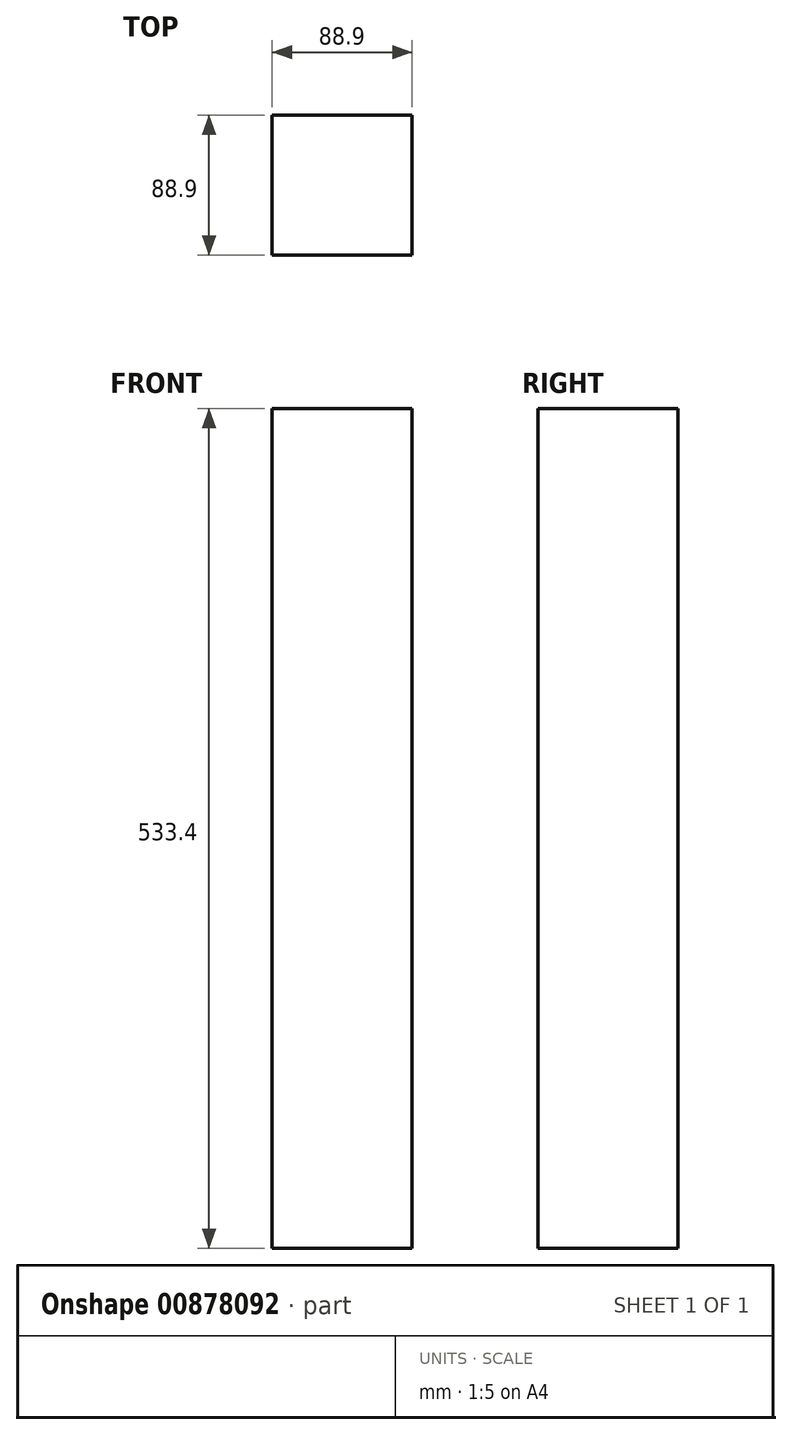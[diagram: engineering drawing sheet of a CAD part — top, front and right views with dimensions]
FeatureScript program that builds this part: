
annotation { "Feature Type Name" : "Feature", "Feature Type Description" : "" }
export const myFeature = defineFeature(function(context is Context, id is Id, definition is map)
    precondition{}
    {
        {
            var Q0;
            Q0=qCreatedBy(makeId("Top.planeOp"),FACE);
            var sketch = newSketch(context, id + "F0", { "sketchPlane" : qUnion([Q0])});
            skLineSegment(sketch, "E0.bottom", {"start": v(44.45, 44.45) * mm, "end": v(-44.45, 44.45) * mm});
            skLineSegment(sketch, "E0.top", {"start": v(44.45, -44.45) * mm, "end": v(-44.45, -44.45) * mm});
            skLineSegment(sketch, "E0.left", {"start": v(44.45, 44.45) * mm, "end": v(44.45, -44.45) * mm});
            skLineSegment(sketch, "E0.right", {"start": v(-44.45, 44.45) * mm, "end": v(-44.45, -44.45) * mm});
            skPoint(sketch, "E0.middle", {"position": v(0, 0) * mm});
            skSolve(sketch);
        }
        {
            var Q0;
            Q0=makeQuery(id+"F0.imprint","IMPRINT",FACE,{"disambiguationData":[TD([[makeQuery(id+"F0.imprint","IMPRINT",EDGE,{"derivedFrom":sQuery(id+"F0.wireOp",EDGE,"E0.bottom")}),1.0]])]});
            extrude(context, id + "F1", {"entities" : qUnion([Q0]), "endBound" : BoundingType.SYMMETRIC, "depth" : 533.4 * mm, "offsetDistance" : 25.4 * mm});
        }
    });
